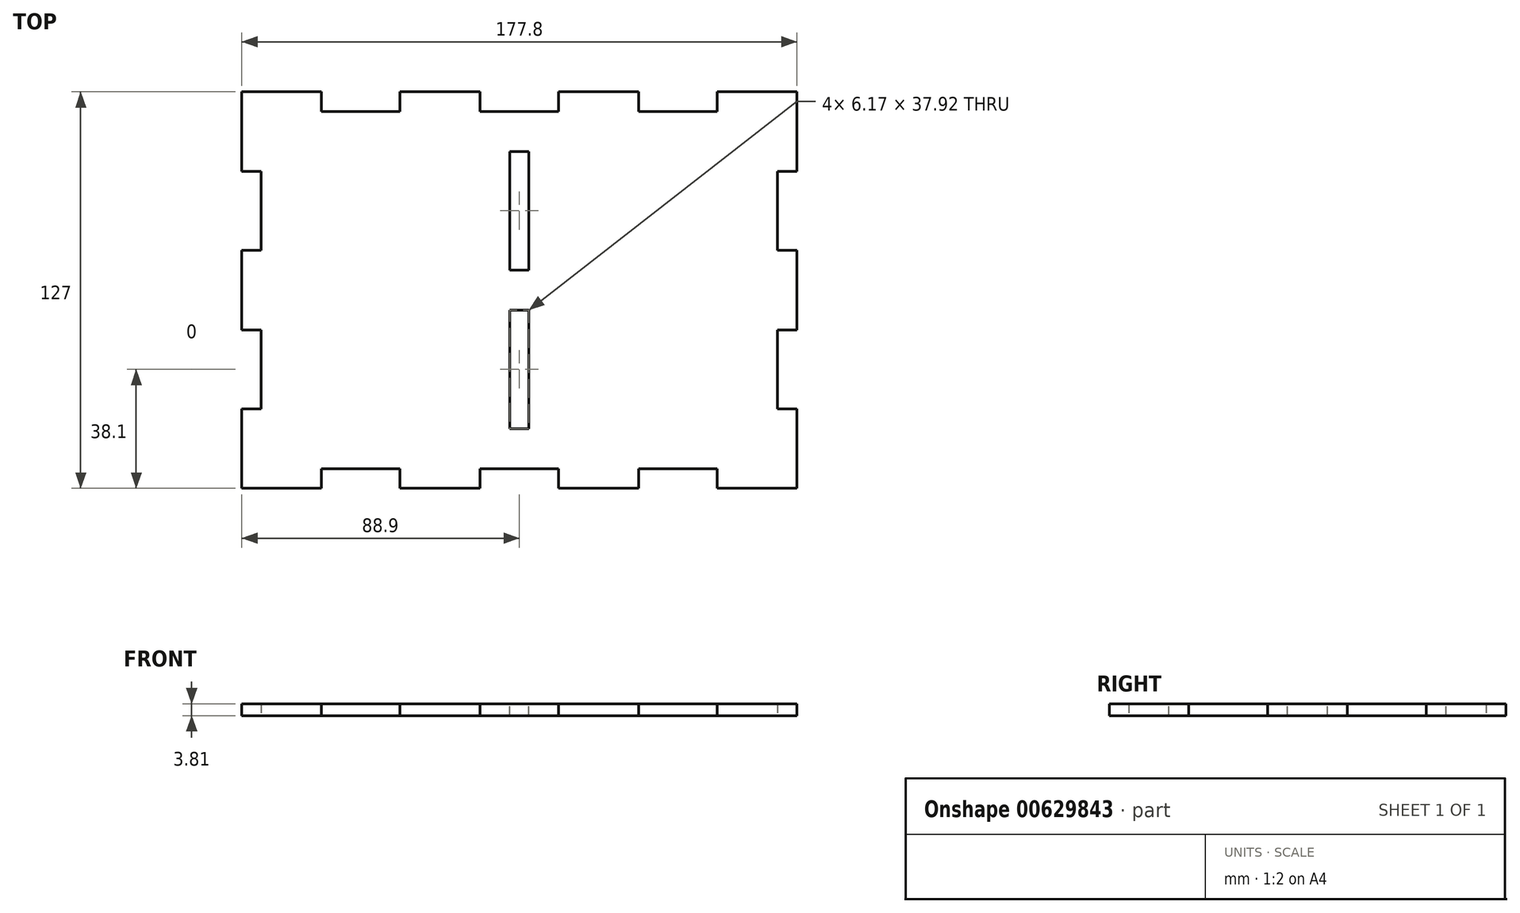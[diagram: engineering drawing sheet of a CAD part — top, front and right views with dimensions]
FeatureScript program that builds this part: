
annotation { "Feature Type Name" : "Feature", "Feature Type Description" : "" }
export const myFeature = defineFeature(function(context is Context, id is Id, definition is map)
    precondition{}
    {
        {
            var Q0;
            Q0=qCreatedBy(makeId("Top.planeOp"),FACE);
            var sketch = newSketch(context, id + "F0", { "sketchPlane" : qUnion([Q0])});
            skLineSegment(sketch, "E0.bottom", {"start": v(0, 127) * mm, "end": v(177.8, 127) * mm});
            skLineSegment(sketch, "E0.top", {"start": v(0, 0) * mm, "end": v(177.8, 0) * mm});
            skLineSegment(sketch, "E0.left", {"start": v(0, 127) * mm, "end": v(0, 0) * mm});
            skLineSegment(sketch, "E0.right", {"start": v(177.8, 127) * mm, "end": v(177.8, 0) * mm});
            skLineSegment(sketch, "E1.bottom", {"start": v(25.49, 0) * mm, "end": v(50.71, 0) * mm});
            skLineSegment(sketch, "E1.top", {"start": v(25.49, 6.26) * mm, "end": v(50.71, 6.26) * mm});
            skLineSegment(sketch, "E1.left", {"start": v(25.49, 0) * mm, "end": v(25.49, 6.26) * mm});
            skLineSegment(sketch, "E1.right", {"start": v(50.71, 0) * mm, "end": v(50.71, 6.26) * mm});
            skPoint(sketch, "E2", {"position": v(38.1, 6.26) * mm});
            skPoint(sketch, "E3.1.0.0", {"position": v(88.9, 6.26) * mm});
            skLineSegment(sketch, "E3.1.0.1", {"start": v(101.51, 0) * mm, "end": v(101.51, 6.26) * mm});
            skLineSegment(sketch, "E3.1.0.2", {"start": v(76.29, 0) * mm, "end": v(76.29, 6.26) * mm});
            skLineSegment(sketch, "E3.1.0.3", {"start": v(76.29, 6.26) * mm, "end": v(101.51, 6.26) * mm});
            skPoint(sketch, "E3.2.0.0", {"position": v(139.7, 6.26) * mm});
            skLineSegment(sketch, "E3.2.0.1", {"start": v(152.31, 0) * mm, "end": v(152.31, 6.26) * mm});
            skLineSegment(sketch, "E3.2.0.2", {"start": v(127.09, 0) * mm, "end": v(127.09, 6.26) * mm});
            skLineSegment(sketch, "E3.2.0.3", {"start": v(127.09, 6.26) * mm, "end": v(152.31, 6.26) * mm});
            skLineSegment(sketch, "E3.direction1", {"start": v(38.1, 6.26) * mm, "end": v(88.9, 6.26) * mm, "construction": true});
            skLineSegment(sketch, "E4.bottom", {"start": v(177.8, 50.71) * mm, "end": v(171.54, 50.71) * mm});
            skLineSegment(sketch, "E4.top", {"start": v(177.8, 25.49) * mm, "end": v(171.54, 25.49) * mm});
            skLineSegment(sketch, "E4.left", {"start": v(177.8, 50.71) * mm, "end": v(177.8, 25.49) * mm});
            skLineSegment(sketch, "E4.right", {"start": v(171.54, 50.71) * mm, "end": v(171.54, 25.49) * mm});
            skPoint(sketch, "E5", {"position": v(171.54, 38.1) * mm});
            skPoint(sketch, "E6.0.1.0", {"position": v(171.54, 88.9) * mm});
            skLineSegment(sketch, "E6.0.1.1", {"start": v(171.54, 101.51) * mm, "end": v(171.54, 76.29) * mm});
            skLineSegment(sketch, "E6.0.1.2", {"start": v(177.8, 101.51) * mm, "end": v(171.54, 101.51) * mm});
            skLineSegment(sketch, "E6.0.1.3", {"start": v(177.8, 101.51) * mm, "end": v(177.8, 76.29) * mm});
            skLineSegment(sketch, "E6.0.1.4", {"start": v(177.8, 76.29) * mm, "end": v(171.54, 76.29) * mm});
            skLineSegment(sketch, "E6.direction1", {"start": v(171.54, 38.1) * mm, "end": v(206.08, 38.1) * mm, "construction": true});
            skLineSegment(sketch, "E6.direction2", {"start": v(171.54, 38.1) * mm, "end": v(171.54, 88.9) * mm, "construction": true});
            skLineSegment(sketch, "E7", {"start": v(0, 63.5) * mm, "end": v(177.8, 63.5) * mm, "construction": true});
            skLineSegment(sketch, "E8", {"start": v(88.9, 127) * mm, "end": v(88.9, 0) * mm, "construction": true});
            skLineSegment(sketch, "E9.MirrorCS", {"start": v(25.49, 120.74) * mm, "end": v(50.71, 120.74) * mm});
            skLineSegment(sketch, "E10.MirrorCS", {"start": v(25.49, 127) * mm, "end": v(25.49, 120.74) * mm});
            skLineSegment(sketch, "E11.MirrorCS", {"start": v(50.71, 127) * mm, "end": v(50.71, 120.74) * mm});
            skLineSegment(sketch, "E12.MirrorCS", {"start": v(25.49, 127) * mm, "end": v(50.71, 127) * mm});
            skLineSegment(sketch, "E13.MirrorCS", {"start": v(76.29, 127) * mm, "end": v(76.29, 120.74) * mm});
            skLineSegment(sketch, "E14.MirrorCS", {"start": v(38.1, 120.74) * mm, "end": v(88.9, 120.74) * mm, "construction": true});
            skLineSegment(sketch, "E15.MirrorCS", {"start": v(76.29, 120.74) * mm, "end": v(101.51, 120.74) * mm});
            skLineSegment(sketch, "E16.MirrorCS", {"start": v(101.51, 127) * mm, "end": v(101.51, 120.74) * mm});
            skLineSegment(sketch, "E17.MirrorCS", {"start": v(127.09, 120.74) * mm, "end": v(152.31, 120.74) * mm});
            skLineSegment(sketch, "E18.MirrorCS", {"start": v(127.09, 127) * mm, "end": v(127.09, 120.74) * mm});
            skLineSegment(sketch, "E19.MirrorCS", {"start": v(152.31, 127) * mm, "end": v(152.31, 120.74) * mm});
            skLineSegment(sketch, "E20.MirrorCS", {"start": v(0, 101.51) * mm, "end": v(6.26, 101.51) * mm});
            skLineSegment(sketch, "E21.MirrorCS", {"start": v(6.26, 101.51) * mm, "end": v(6.26, 76.29) * mm});
            skLineSegment(sketch, "E22.MirrorCS", {"start": v(0, 76.29) * mm, "end": v(6.26, 76.29) * mm});
            skLineSegment(sketch, "E23.MirrorCS", {"start": v(0, 101.51) * mm, "end": v(0, 76.29) * mm});
            skLineSegment(sketch, "E24.MirrorCS", {"start": v(0, 50.71) * mm, "end": v(6.26, 50.71) * mm});
            skLineSegment(sketch, "E25.MirrorCS", {"start": v(6.26, 38.1) * mm, "end": v(6.26, 88.9) * mm, "construction": true});
            skLineSegment(sketch, "E26.MirrorCS", {"start": v(0, 25.49) * mm, "end": v(6.26, 25.49) * mm});
            skLineSegment(sketch, "E27.MirrorCS", {"start": v(0, 50.71) * mm, "end": v(0, 25.49) * mm});
            skLineSegment(sketch, "E28.MirrorCS", {"start": v(6.26, 50.71) * mm, "end": v(6.26, 25.49) * mm});
            skSolve(sketch);
        }
        {
            var Q0;
            Q0=makeQuery(id+"F0.imprint","IMPRINT",FACE,{"disambiguationData":[TD([[makeQuery(id+"F0.imprint","IMPRINT",EDGE,{"derivedFrom":sQuery(id+"F0.wireOp",EDGE,"E1.top")}),1.0]])]});
            extrude(context, id + "F1", {"entities" : qUnion([Q0]), "depth" : 3.8 * mm, "offsetDistance" : 25.4 * mm});
        }
        {
            var Q0;
            Q0=makeQuery(id+"F1.opExtrude","CAP_FACE",FACE,{"disambiguationData":[OSD([sQuery(id+"F0.wireOp",EDGE,"E0.top"),sQuery(id+"F0.wireOp",EDGE,"E0.left"),sQuery(id+"F0.wireOp",EDGE,"E0.right"),sQuery(id+"F0.wireOp",EDGE,"E1.top"),sQuery(id+"F0.wireOp",EDGE,"E1.left"),sQuery(id+"F0.wireOp",EDGE,"E1.right"),sQuery(id+"F0.wireOp",EDGE,"E3.1.0.1"),sQuery(id+"F0.wireOp",EDGE,"E3.1.0.2"),sQuery(id+"F0.wireOp",EDGE,"E3.1.0.3"),sQuery(id+"F0.wireOp",EDGE,"E3.2.0.1"),sQuery(id+"F0.wireOp",EDGE,"E3.2.0.2"),sQuery(id+"F0.wireOp",EDGE,"E3.2.0.3"),sQuery(id+"F0.wireOp",EDGE,"E4.bottom"),sQuery(id+"F0.wireOp",EDGE,"E4.top"),sQuery(id+"F0.wireOp",EDGE,"E4.right"),sQuery(id+"F0.wireOp",EDGE,"E6.0.1.1"),sQuery(id+"F0.wireOp",EDGE,"E6.0.1.2"),sQuery(id+"F0.wireOp",EDGE,"E6.0.1.4"),sQuery(id+"F0.wireOp",EDGE,"E9.MirrorCS"),sQuery(id+"F0.wireOp",EDGE,"E10.MirrorCS"),sQuery(id+"F0.wireOp",EDGE,"E11.MirrorCS"),sQuery(id+"F0.wireOp",EDGE,"E13.MirrorCS"),sQuery(id+"F0.wireOp",EDGE,"E15.MirrorCS"),sQuery(id+"F0.wireOp",EDGE,"E16.MirrorCS"),sQuery(id+"F0.wireOp",EDGE,"E17.MirrorCS"),sQuery(id+"F0.wireOp",EDGE,"E18.MirrorCS"),sQuery(id+"F0.wireOp",EDGE,"E19.MirrorCS"),sQuery(id+"F0.wireOp",EDGE,"E0.bottom"),sQuery(id+"F0.wireOp",EDGE,"E20.MirrorCS"),sQuery(id+"F0.wireOp",EDGE,"E21.MirrorCS"),sQuery(id+"F0.wireOp",EDGE,"E22.MirrorCS"),sQuery(id+"F0.wireOp",EDGE,"E24.MirrorCS"),sQuery(id+"F0.wireOp",EDGE,"E26.MirrorCS"),sQuery(id+"F0.wireOp",EDGE,"E28.MirrorCS")])],"isStart":false});
            var sketch = newSketch(context, id + "F2", { "sketchPlane" : qUnion([Q0])});
            skLineSegment(sketch, "E29.bottom", {"start": v(85.81, 107.86) * mm, "end": v(91.99, 107.86) * mm});
            skLineSegment(sketch, "E29.top", {"start": v(85.81, 69.94) * mm, "end": v(91.99, 69.94) * mm});
            skLineSegment(sketch, "E29.left", {"start": v(85.81, 107.86) * mm, "end": v(85.81, 69.94) * mm});
            skLineSegment(sketch, "E29.right", {"start": v(91.99, 107.86) * mm, "end": v(91.99, 69.94) * mm});
            skLineSegment(sketch, "E30.bottom", {"start": v(85.81, 57.06) * mm, "end": v(91.99, 57.06) * mm});
            skLineSegment(sketch, "E30.top", {"start": v(85.81, 19.14) * mm, "end": v(91.99, 19.14) * mm});
            skLineSegment(sketch, "E30.left", {"start": v(85.81, 57.06) * mm, "end": v(85.81, 19.14) * mm});
            skLineSegment(sketch, "E30.right", {"start": v(91.99, 57.06) * mm, "end": v(91.99, 19.14) * mm});
            skPoint(sketch, "E31", {"position": v(91.99, 88.9) * mm});
            skPoint(sketch, "E32", {"position": v(91.99, 38.1) * mm});
            skPoint(sketch, "E33", {"position": v(88.9, 19.14) * mm});
            skPoint(sketch, "E34", {"position": v(88.9, 69.94) * mm});
            skPoint(sketch, "E35", {"position": v(88.9, 6.26) * mm});
            skSolve(sketch);
        }
        {
            var Q0;
            Q0 = qSketchRegion(id + "F2", true);
            extrude(context, id + "F3", {"entities" : qUnion([Q0]), "operationType" : NewBodyOperationType.REMOVE, "endBound" : BoundingType.THROUGH_ALL, "oppositeDirection" : true, "depth" : 25.4 * mm, "offsetDistance" : 25.4 * mm});
        }
    });
